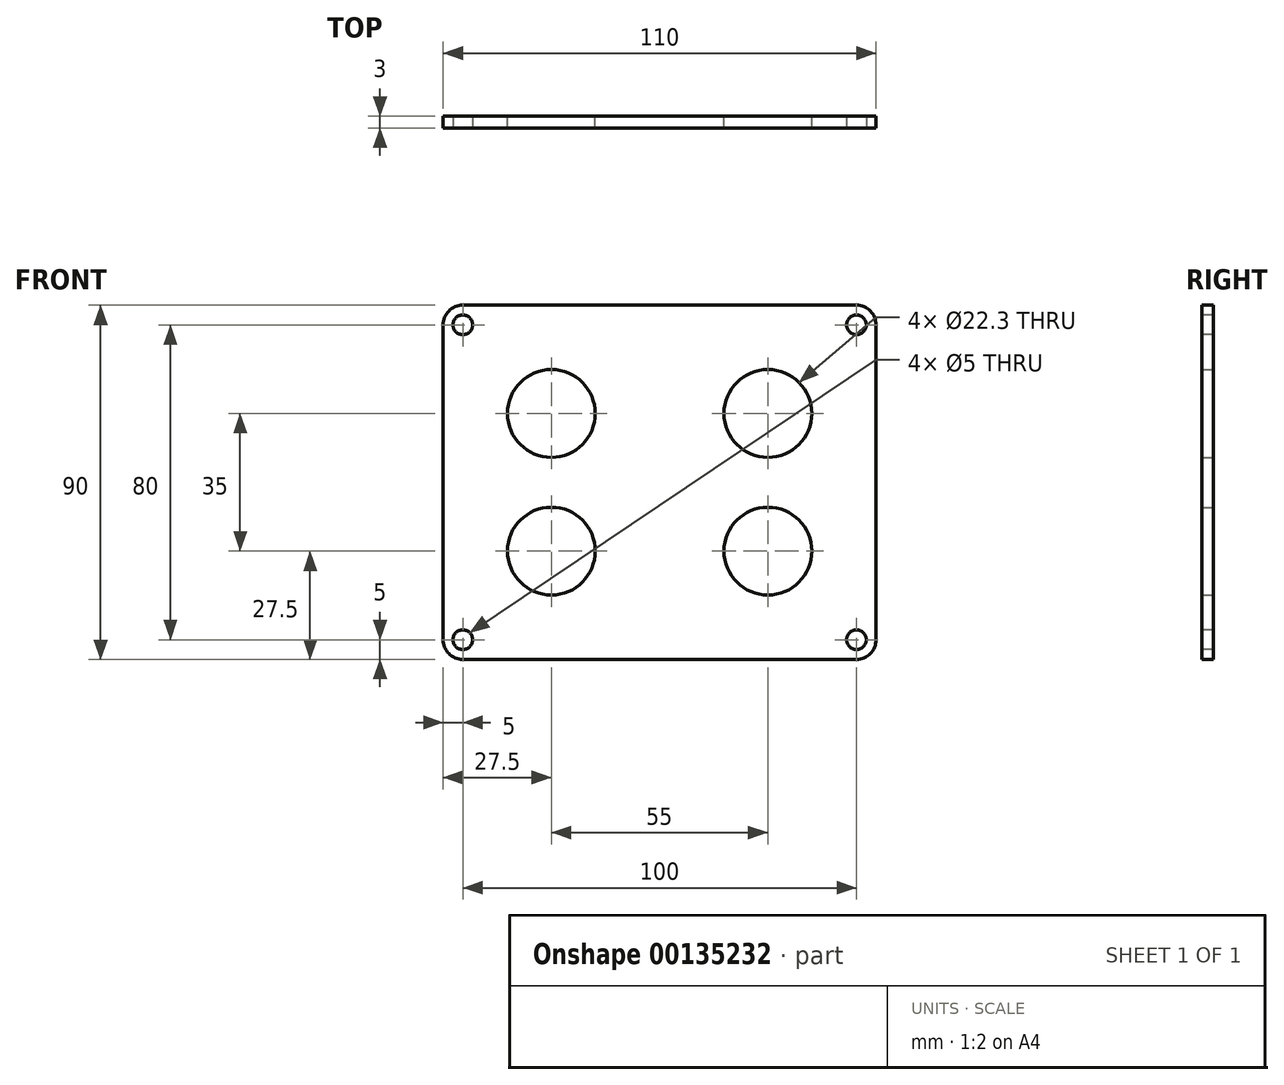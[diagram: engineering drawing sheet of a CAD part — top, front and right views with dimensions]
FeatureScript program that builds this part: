
annotation { "Feature Type Name" : "Feature", "Feature Type Description" : "" }
export const myFeature = defineFeature(function(context is Context, id is Id, definition is map)
    precondition{}
    {
        {
            var Q0;
            Q0=qCreatedBy(makeId("Front.planeOp"),FACE);
            var sketch = newSketch(context, id + "F0", { "sketchPlane" : qUnion([Q0])});
            skLineSegment(sketch, "E0.bottom", {"start": v(55, -45) * mm, "end": v(-55, -45) * mm});
            skLineSegment(sketch, "E0.top", {"start": v(55, 45) * mm, "end": v(-55, 45) * mm});
            skLineSegment(sketch, "E0.left", {"start": v(55, -45) * mm, "end": v(55, 45) * mm});
            skLineSegment(sketch, "E0.right", {"start": v(-55, -45) * mm, "end": v(-55, 45) * mm});
            skPoint(sketch, "E0.middle", {"position": v(0, 0) * mm});
            skCircle(sketch, "E1", {"center": v(27.5, 17.5) * mm, "radius": 11.15 * mm});
            skCircle(sketch, "E2", {"center": v(27.5, -17.5) * mm, "radius": 11.15 * mm});
            skCircle(sketch, "E3", {"center": v(-27.5, -17.5) * mm, "radius": 11.15 * mm});
            skCircle(sketch, "E4", {"center": v(-27.5, 17.5) * mm, "radius": 11.15 * mm});
            skSolve(sketch);
        }
        {
            var Q0;
            Q0=makeQuery(id+"F0.imprint","IMPRINT",FACE,{"disambiguationData":[TD([[makeQuery(id+"F0.imprint","IMPRINT",EDGE,{"derivedFrom":sQuery(id+"F0.wireOp",EDGE,"E0.bottom")}),-1.0]])]});
            extrude(context, id + "F1", {"entities" : qUnion([Q0]), "depth" : 3 * mm});
        }
        {
            var Q0;
            Q0=makeQuery(id+"F1.opExtrude","CAP_FACE",FACE,{"disambiguationData":[OSD([sQuery(id+"F0.wireOp",EDGE,"E0.bottom"),sQuery(id+"F0.wireOp",EDGE,"E0.top"),sQuery(id+"F0.wireOp",EDGE,"E0.left"),sQuery(id+"F0.wireOp",EDGE,"E0.right"),sQuery(id+"F0.wireOp",EDGE,"snz76OHE-M62r-xchw-LMaD-d34flNXxoI04"),sQuery(id+"F0.wireOp",EDGE,"YiBMRkDV-long-l9aM-QcSy-laY2PdDEb2Ov"),sQuery(id+"F0.wireOp",EDGE,"OeKSNgk5-mpKf-t9Wr-nT9t-RBBhHM6Q2Nae")])],"isStart":false});
            var sketch = newSketch(context, id + "F2", { "sketchPlane" : qUnion([Q0])});
            skCircle(sketch, "E5", {"center": v(-50, 40) * mm, "radius": 2.5 * mm});
            skCircle(sketch, "E6", {"center": v(50, 40) * mm, "radius": 2.5 * mm});
            skCircle(sketch, "E7", {"center": v(50, -40) * mm, "radius": 2.5 * mm});
            skCircle(sketch, "E8", {"center": v(-50, -40) * mm, "radius": 2.5 * mm});
            skSolve(sketch);
        }
        {
            var Q0;
            Q0=qSketchRegion(id+"F2",true);
            extrude(context, id + "F3", {"entities" : qUnion([Q0]), "operationType" : NewBodyOperationType.REMOVE, "endBound" : BoundingType.UP_TO_NEXT, "oppositeDirection" : true, "depth" : 25 * mm});
        }
        {
            var Q0;
            Q0=makeQuery(id+"F1.opExtrude","SWEPT_EDGE",EDGE,{"disambiguationData":[OSD([sQuery(id+"F0.wireOp",EDGE,"E0.top"),sQuery(id+"F0.wireOp",EDGE,"E0.left")])]});
            var Q1;
            Q1=makeQuery(id+"F1.opExtrude","SWEPT_EDGE",EDGE,{"disambiguationData":[OSD([sQuery(id+"F0.wireOp",EDGE,"E0.top"),sQuery(id+"F0.wireOp",EDGE,"E0.right")])]});
            var Q2;
            Q2=makeQuery(id+"F1.opExtrude","SWEPT_EDGE",EDGE,{"disambiguationData":[OSD([sQuery(id+"F0.wireOp",EDGE,"E0.bottom"),sQuery(id+"F0.wireOp",EDGE,"E0.left")])]});
            var Q3;
            Q3=makeQuery(id+"F1.opExtrude","SWEPT_EDGE",EDGE,{"disambiguationData":[OSD([sQuery(id+"F0.wireOp",EDGE,"E0.bottom"),sQuery(id+"F0.wireOp",EDGE,"E0.right")])]});
            fillet(context, id + "F4", {"entities" : qUnion([Q0, Q1, Q2, Q3]), "radius" : 5 * mm, "tangentPropagation" : true, "allowEdgeOverflow" : false});
        }
    });
